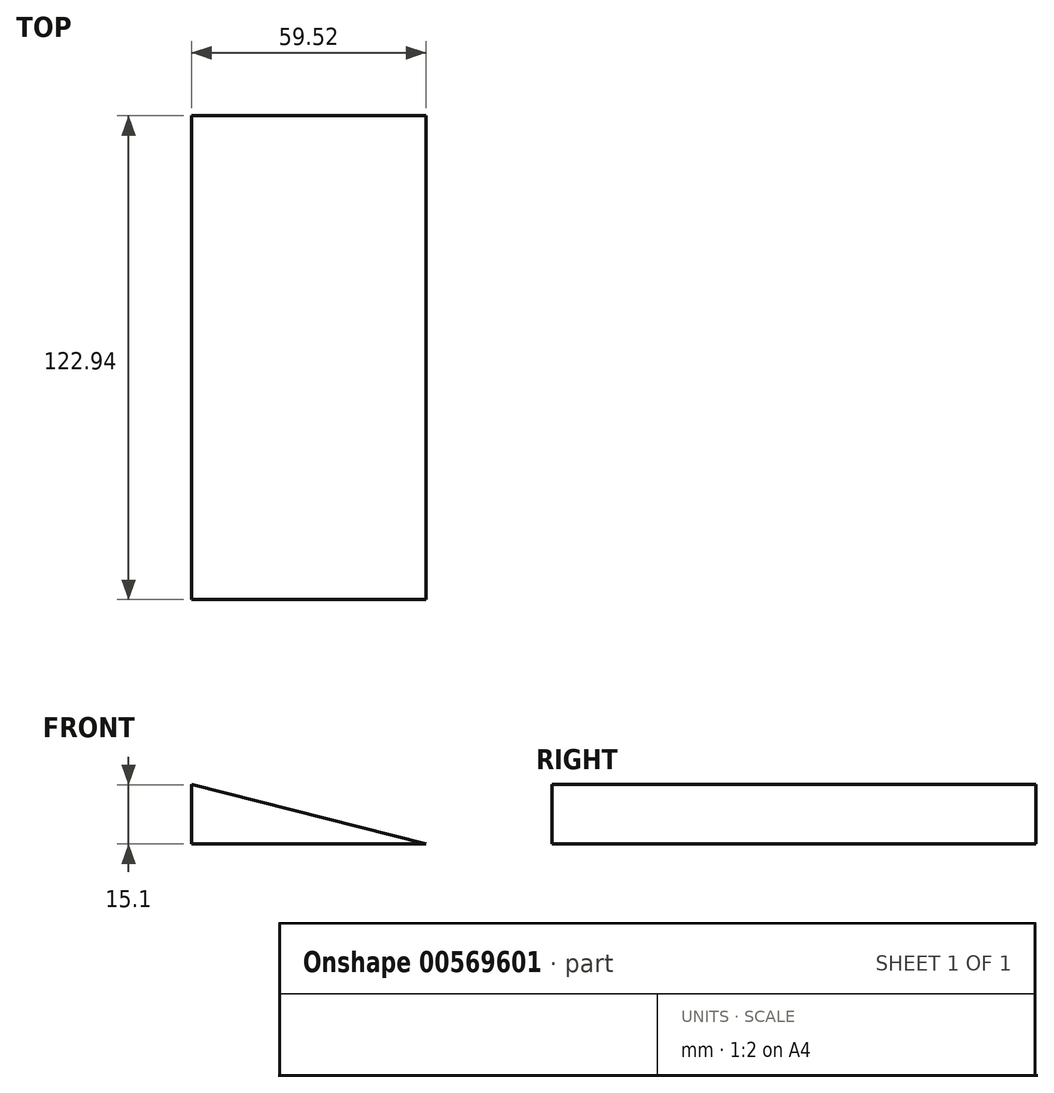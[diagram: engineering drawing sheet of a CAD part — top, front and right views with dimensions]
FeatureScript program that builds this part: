
annotation { "Feature Type Name" : "Feature", "Feature Type Description" : "" }
export const myFeature = defineFeature(function(context is Context, id is Id, definition is map)
    precondition{}
    {
        {
            var Q0;
            Q0=qCreatedBy(makeId("Front.planeOp"),FACE);
            var sketch = newSketch(context, id + "F0", { "sketchPlane" : qUnion([Q0])});
            skLineSegment(sketch, "E0.bottom", {"start": v(-29.76, 7.55) * mm, "end": v(29.76, 7.55) * mm});
            skLineSegment(sketch, "E0.top", {"start": v(-29.76, -7.55) * mm, "end": v(29.76, -7.55) * mm});
            skLineSegment(sketch, "E0.left", {"start": v(-29.76, 7.55) * mm, "end": v(-29.76, -7.55) * mm});
            skLineSegment(sketch, "E0.right", {"start": v(29.76, 7.55) * mm, "end": v(29.76, -7.55) * mm});
            skPoint(sketch, "E0.middle", {"position": v(0, 0) * mm});
            skLineSegment(sketch, "E1", {"start": v(-29.76, 7.55) * mm, "end": v(29.76, -7.55) * mm});
            skSolve(sketch);
        }
        {
            var Q0;
            Q0=makeQuery(id+"F0.imprint","IMPRINT",FACE,{"disambiguationData":[TD([[makeQuery(id+"F0.imprint","IMPRINT",EDGE,{"derivedFrom":sQuery(id+"F0.wireOp",EDGE,"E0.top")}),1.0]])]});
            extrude(context, id + "F1", {"entities" : qUnion([Q0]), "depth" : 122.94 * mm, "offsetDistance" : 25.4 * mm});
        }
    });
